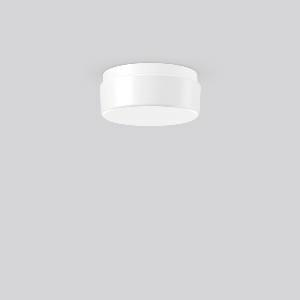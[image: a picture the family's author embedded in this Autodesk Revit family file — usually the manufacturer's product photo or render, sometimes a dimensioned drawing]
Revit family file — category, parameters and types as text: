
# Revit family: kreis_211416_002_13e0
name_source: partatom
category: Lighting Fixtures
units: mm (PartAtom-declared; Revit-internal decimal feet)

## family parameters
Cut with Voids When Loaded = No
Host = Face
Light Source = No
Part Type = Normal
Room Calculation Point = No
Round Connector Dimension = Use Diameter
Shared = No

## types (1)
- KREIS (1 x LED Modul 830, 1150 lm, 3000)
    Apparent Load = 12 VA
    CIE Flux Codes = 38 68 88 79 100
    Color Rendering = 80
    Color Temperature = 3000
    Default Elevation = 1800 mm
    Description = Series: KREIS
Round surface-mounted luminaire in classic design. Base: plastic. Opal glass: mouth-blown, satin finish. Diffuser fastening: spring system. Suitable for Ceiling mounting, Wall (surface). IP 43 ceiling mounting, IP 44 wall mounting. 
Colour: white
Diameter: 280 mm
Height: 120 mm
Lamp: LED exchangeable
Socket: without socket
Colour temperature: 3000K
Colour rendering index (CRI): 83
System power: 12 W
Rated luminous flux: 1150 lm
Luminous efficiency: 96 lm/W
Control gear: AC Strom, dim.Ph.an-/abschnitt
Protection class: I
Type of protection: IP 43
    Height = 120 mm
    Lamp = 1 x LED Modul 830
    Lamp Light Flux = 1150 lm
    Lamp count = 1
    Length = 280 mm
    Lifetime = 50000 h
    Luminous efficacy = 96 lm/W
    Manufacturer = RZB
    ModVariant = No
    Model = 211416.002
    Mounting Place = Wall, Ceiling
    Mounting Type = Surface mounted
    Number of Poles = 1
    OnlyDefault = Yes
    Power Factor = 1
    Product Name = KREIS
    Product group = Surface mounted ceiling and wall luminaires
    ProductGroupID = 305
    Protection Class = Protection class I
    Protection Degree = IP 43
    RLX_Detail_Level = 1
    RLX_Emergency_Light_Flux = 0 lm
    RLX_Emergency_Type = 0
    RLX_Emergency_Type_DB = No
    RlxData = <blob elided: 11633 chars, md5=502064d9>
    Socket = socket
    Standby Power = 0 W
    System Light Flux = 1150 lm
    System Power = 12 W
    Type Comments = Product without accessories
    Type Image = 21171.002.jpg
    URL = http://relux.com
    VarID = ---
    Voltage = 230 V
    Voltage Range = 220-240 V
    Weight = 0.00 kg
    Width = 0 mm  [stored 0 ft]

note: [stored X ft] marks values corroborated as IEEE doubles in the binary element streams (Revit-internal decimal feet)

## geometry (parser evidence)
native form markers: Sweep x12
no freeform markers — native parametric forms only
